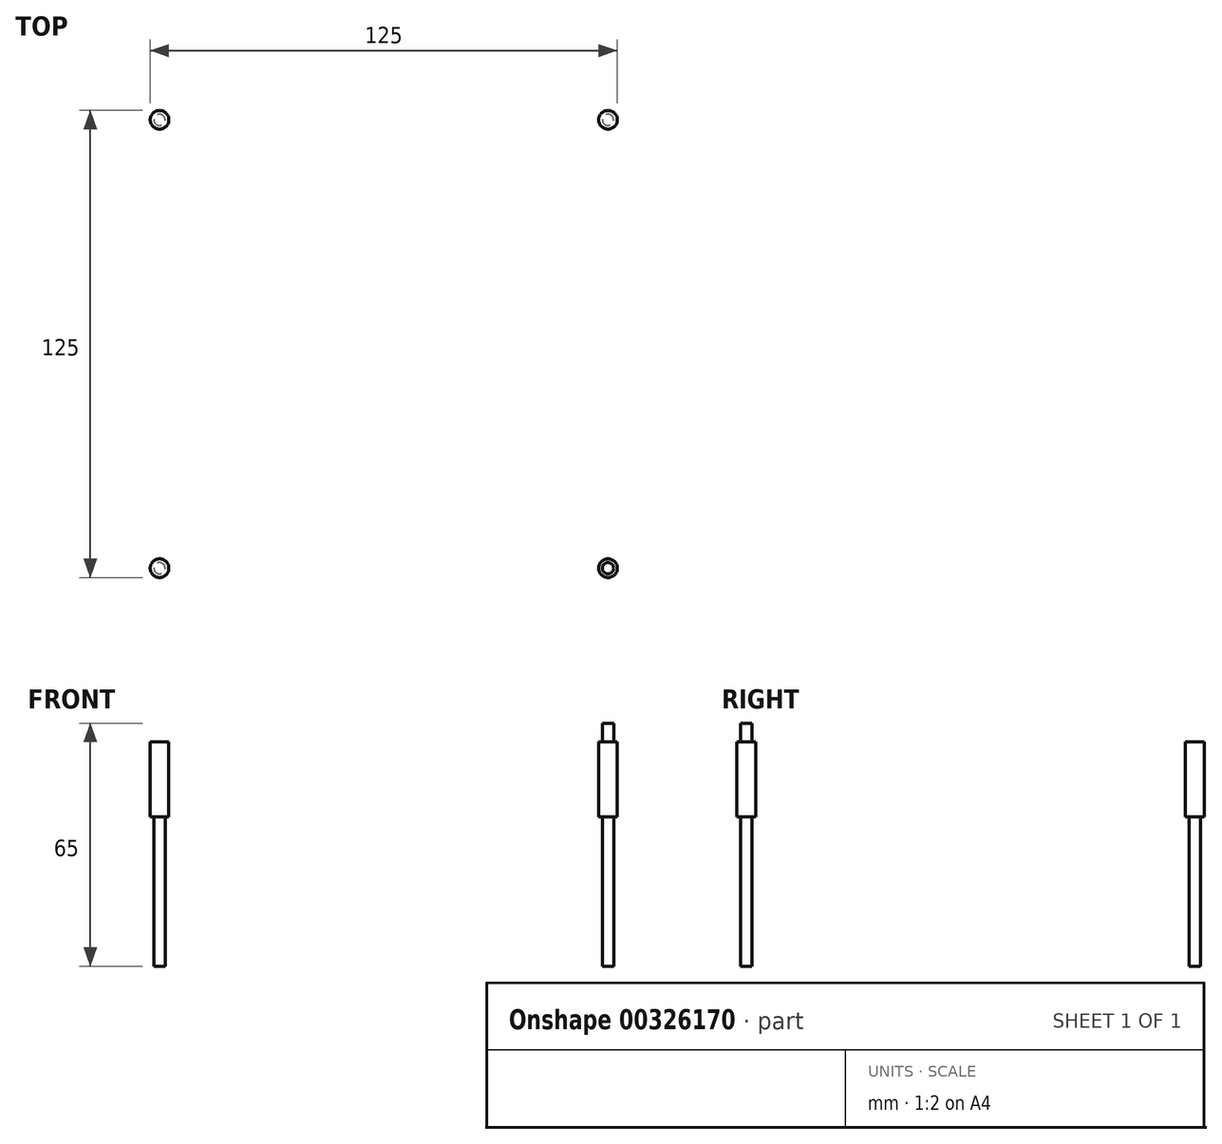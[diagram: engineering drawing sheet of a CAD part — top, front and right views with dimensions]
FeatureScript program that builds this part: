
annotation { "Feature Type Name" : "Feature", "Feature Type Description" : "" }
export const myFeature = defineFeature(function(context is Context, id is Id, definition is map)
    precondition{}
    {
        {
            var Q0;
            Q0=qCreatedBy(makeId("Top.planeOp"),FACE);
            var sketch = newSketch(context, id + "F0", { "sketchPlane" : qUnion([Q0])});
            skLineSegment(sketch, "E0.bottom", {"start": v(60, -60) * mm, "end": v(-60, -60) * mm, "construction": true});
            skLineSegment(sketch, "E0.top", {"start": v(60, 60) * mm, "end": v(-60, 60) * mm, "construction": true});
            skLineSegment(sketch, "E0.left", {"start": v(60, -60) * mm, "end": v(60, 60) * mm, "construction": true});
            skLineSegment(sketch, "E0.right", {"start": v(-60, -60) * mm, "end": v(-60, 60) * mm, "construction": true});
            skPoint(sketch, "E0.middle", {"position": v(0, 0) * mm});
            skCircle(sketch, "E1", {"center": v(60, -60) * mm, "radius": 1.5 * mm});
            skCircle(sketch, "E2", {"center": v(60, -60) * mm, "radius": 2.5 * mm});
            skSolve(sketch);
        }
        {
            var Q0;
            Q0=makeQuery(id+"F0.imprint","IMPRINT",FACE,{"disambiguationData":[TD([[makeQuery(id+"F0.imprint","IMPRINT",EDGE,{"derivedFrom":sQuery(id+"F0.wireOp",EDGE,"E1")}),1.0]])]});
            extrude(context, id + "F1", {"entities" : qUnion([Q0]), "oppositeDirection" : true, "depth" : 40 * mm});
        }
        {
            var Q0;
            Q0=makeQuery(id+"F0.imprint","IMPRINT",FACE,{"disambiguationData":[TD([[makeQuery(id+"F0.imprint","IMPRINT",EDGE,{"derivedFrom":sQuery(id+"F0.wireOp",EDGE,"E1")}),-1.0]])]});
            var Q1;
            Q1=makeQuery(id+"F0.imprint","IMPRINT",FACE,{"disambiguationData":[TD([[makeQuery(id+"F0.imprint","IMPRINT",EDGE,{"derivedFrom":sQuery(id+"F0.wireOp",EDGE,"E1")}),1.0]])]});
            extrude(context, id + "F2", {"entities" : qUnion([Q0, Q1]), "operationType" : NewBodyOperationType.ADD, "depth" : 20 * mm});
        }
        {
            var Q0;
            Q0=qCreatedBy(makeId("Right.planeOp"),FACE);
            var sketch = newSketch(context, id + "F3", { "sketchPlane" : qUnion([Q0])});
            skLineSegment(sketch, "E3", {"start": v(0, 0) * mm, "end": v(0, 50) * mm, "construction": true});
            skSolve(sketch);
        }
        {
            var Q0;
            Q0=makeQuery(id+"F1.opExtrude","SWEPT_BODY",BODY,{"disambiguationData":[OSD([sQuery(id+"F0.wireOp",EDGE,"E1")])]});
            var Q1;
            Q1=sQuery(id+"F3.wireOp",EDGE,"E3");
            circularPattern(context, id + "F4", {"entities" : qUnion([Q0]), "axis" : qUnion([Q1]), "angle" : 360 * degree, "instanceCount" : 4, "equalSpace" : true, "computeTransformsWithoutBuiltin" : true});
        }
        {
            var Q0;
            Q0=makeQuery(id+"F0.imprint","IMPRINT",FACE,{"disambiguationData":[TD([[makeQuery(id+"F0.imprint","IMPRINT",EDGE,{"derivedFrom":sQuery(id+"F0.wireOp",EDGE,"E1")}),1.0]])]});
            extrude(context, id + "F5", {"entities" : qUnion([Q0]), "operationType" : NewBodyOperationType.ADD, "depth" : 25 * mm});
        }
    });
